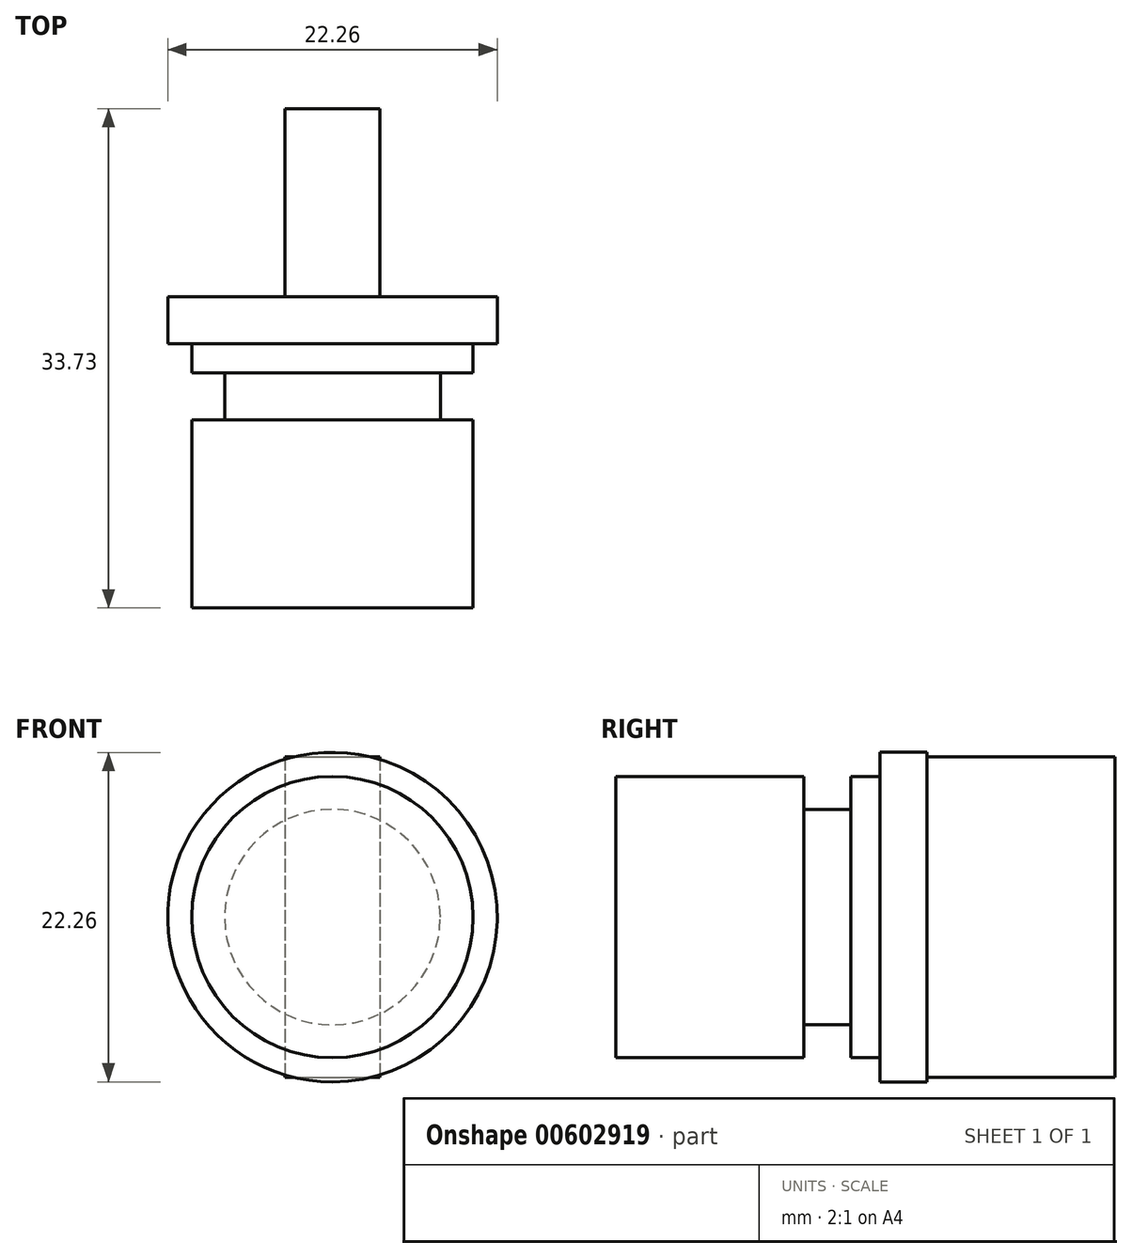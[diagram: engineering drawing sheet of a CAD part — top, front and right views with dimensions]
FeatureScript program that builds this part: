
annotation { "Feature Type Name" : "Feature", "Feature Type Description" : "" }
export const myFeature = defineFeature(function(context is Context, id is Id, definition is map)
    precondition{}
    {
        {
            var Q0;
            Q0=qCreatedBy(makeId("Front.planeOp"),FACE);
            var sketch = newSketch(context, id + "F0", { "sketchPlane" : qUnion([Q0])});
            skCircle(sketch, "E0", {"center": v(0, 0) * mm, "radius": 11.13 * mm});
            skSolve(sketch);
        }
        {
            var Q0;
            Q0 = qSketchRegion(id + "F0", true);
            extrude(context, id + "F1", {"entities" : qUnion([Q0]), "depth" : 3.17 * mm, "offsetDistance" : 25.4 * mm});
        }
        {
            var Q0;
            Q0=qCreatedBy(makeId("Front.planeOp"),FACE);
            var sketch = newSketch(context, id + "F2", { "sketchPlane" : qUnion([Q0])});
            skLineSegment(sketch, "E1.bottom", {"start": v(-3.2, 10.83) * mm, "end": v(3.2, 10.83) * mm});
            skLineSegment(sketch, "E1.top", {"start": v(-3.2, -10.83) * mm, "end": v(3.2, -10.83) * mm});
            skLineSegment(sketch, "E1.left", {"start": v(-3.2, 10.83) * mm, "end": v(-3.2, -10.83) * mm});
            skLineSegment(sketch, "E1.right", {"start": v(3.2, 10.83) * mm, "end": v(3.2, -10.83) * mm});
            skPoint(sketch, "E1.middle", {"position": v(0, 0) * mm});
            skSolve(sketch);
        }
        {
            var Q0;
            Q0 = qSketchRegion(id + "F2", true);
            extrude(context, id + "F3", {"entities" : qUnion([Q0]), "operationType" : NewBodyOperationType.ADD, "oppositeDirection" : true, "depth" : 12.7 * mm, "offsetDistance" : 25.4 * mm});
        }
        {
            var Q0;
            Q0=qCreatedBy(makeId("Front.planeOp"),FACE);
            var sketch = newSketch(context, id + "F4", { "sketchPlane" : qUnion([Q0])});
            skCircle(sketch, "E2", {"center": v(0, 0) * mm, "radius": 9.48 * mm});
            skSolve(sketch);
        }
        {
            var Q0;
            Q0 = qSketchRegion(id + "F4", true);
            extrude(context, id + "F5", {"entities" : qUnion([Q0]), "operationType" : NewBodyOperationType.ADD, "depth" : 5.16 * mm, "offsetDistance" : 25.4 * mm});
        }
        {
            var Q0;
            Q0=qCreatedBy(makeId("Front.planeOp"),FACE);
            var sketch = newSketch(context, id + "F6", { "sketchPlane" : qUnion([Q0])});
            skCircle(sketch, "E3", {"center": v(0, 0) * mm, "radius": 7.28 * mm});
            skSolve(sketch);
        }
        {
            var Q0;
            Q0 = qSketchRegion(id + "F6", true);
            extrude(context, id + "F7", {"entities" : qUnion([Q0]), "operationType" : NewBodyOperationType.ADD, "depth" : 8.33 * mm, "offsetDistance" : 25.4 * mm});
        }
        {
            var Q0;
            Q0=makeQuery(id+"F7.opExtrude","CAP_FACE",FACE,{"disambiguationData":[OSD([sQuery(id+"F6.wireOp",EDGE,"E3")])],"isStart":false});
            var sketch = newSketch(context, id + "F8", { "sketchPlane" : qUnion([Q0])});
            skCircle(sketch, "E4", {"center": v(0, 0) * mm, "radius": 9.5 * mm});
            skSolve(sketch);
        }
        {
            var Q0;
            Q0 = qSketchRegion(id + "F8", true);
            extrude(context, id + "F9", {"entities" : qUnion([Q0]), "operationType" : NewBodyOperationType.ADD, "depth" : 12.7 * mm, "offsetDistance" : 25.4 * mm});
        }
    });
